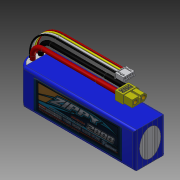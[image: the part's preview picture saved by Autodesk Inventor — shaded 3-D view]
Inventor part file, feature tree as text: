
AUTODESK INVENTOR PART (.ipt)
format: ipt  version: 2014 SP1 (Build 180222100, 222)  size: 2,148,352 bytes
history: native  units: mm
features: sketch x30, extrude x23, plane x4, pattern_linear x3, sweep x3, fillet x2, other x2, emboss x1, projected_geometry x1
ambient origin geometry x8: Origin, YZ Plane, XZ Plane, XY Plane, X Axis, Y Axis, Z Axis, Center Point
bodies: Solid1 (feature_tree)
feature tree (69):
  extrude  "Extrusion1"  Depth=33.0mm
  extrude  "Extrusion2"  Depth=2.0mm
  pattern_linear  "Rectangular Pattern1"  Count1=2 Spacing1=9.333333mm
  fillet  "Fillet1"  Radius=2.0mm
  extrude  "Extrusion3"  Depth=105.0mm TaperAngle=0.0deg
  plane  "Work Plane1"
  extrude  "Extrusion4"  Depth=13.8mm
  extrude  "Extrusion5"  Depth=11.6mm
  extrude  "Extrusion6"  Depth=30.0mm
  extrude  "Extrusion7"  Depth=7.85mm TaperAngle=0.0deg
  extrude  "Extrusion8"  Depth=4.0mm
  extrude  "Extrusion9"  Depth=1.8mm
  plane  "Work Plane2"
  emboss  "Emboss1"
  extrude  "Extrusion10"  Depth=0.75mm
  extrude  "Extrusion11"  Depth=7.6mm TaperAngle=0.0deg
  sketch  "Sketch13"  dims[d32=1.0mm d33=0.0mm d34=1.8mm]
  sketch  "3D Sketch1"
  sweep  "Sweep1"
  sweep  "Sweep2"
  extrude  "Extrusion12"  Depth=60.0mm
  plane  "Work Plane3"
  extrude  "Extrusion13"  Depth=10.0mm TaperAngle=0.0deg
  extrude  "Extrusion14"  Depth=4.3mm
  extrude  "Extrusion15"  Depth=0.3mm TaperAngle=0.0deg
  extrude  "Extrusion16"  Depth=3.5mm
  extrude  "Extrusion17"  Depth=4.0mm
  extrude  "Extrusion18"  Depth=3.9mm
  extrude  "Extrusion19"  Depth=7.8mm
  extrude  "Extrusion20"  Depth=10.0mm
  extrude  "Extrusion21"  Depth=10.0mm
  pattern_linear  "Rectangular Pattern2"  Spacing1=0.0mm  [1 undecoded]
  sketch  "Sketch25"  dims[d74=0.3mm d75=0.0mm d76=3.9mm]
  sweep  "Sweep3"
  pattern_linear  "Rectangular Pattern3"  Spacing1=10.337mm  [1 undecoded]
  extrude  "Extrusion22"  Depth=2.0mm TaperAngle=0.0deg
  plane  "Work Plane4"
  extrude  "Extrusion23"  [1 undecoded]
  fillet  "Fillet4"  Radius=10.6mm
  other  "Decal1"
  sketch  "Sketch1"  dims[d0=28.0mm d1=33.0mm]
  sketch  "Sketch2"  dims[d2=105.0mm d3=0.0mm d4=2.0mm]
  sketch  "Sketch3"  dims[d5=2.0mm]
  sketch  "Sketch4"  dims[d6=28.0mm]
  sketch  "Sketch5"  dims[d7=9.333333mm]
  sketch  "Sketch6"  dims[d8=105.0mm d9=0.0mm d10=20.0mm d12=9.333333mm d13=2.0mm]
  sketch  "Sketch7"  dims[d14=8.0mm d15=105.0mm d16=0.0mm]
  sketch  "Sketch8"  dims[d17=-10.0mm d18=13.8mm]
  sketch  "Sketch9"  dims[d19=6.6mm d20=11.6mm]
  sketch  "Sketch10"  dims[d21=2.2mm d22=30.0mm]
  sketch  "Sketch11"  dims[d26=6.6mm d27=7.85mm d28=0.0mm]
  sketch  "Sketch12"  dims[d29=1.0mm d30=4.0mm]
  sketch  "Sketch14"  dims[d35=1.0mm d36=0.0mm d37=0.75mm]
  sketch  "Sketch15"  dims[d38=0.75mm d39=7.6mm d40=0.0mm]
  sketch  "Sketch16"  dims[d41=10.0mm d42=0.3mm d43=0.0mm]
  sketch  "Sketch17"  dims[d44=0.1mm d45=4.93934mm]
  sketch  "Sketch18"  dims[d46=0.70562mm d54=60.0mm d56=0.70562mm]
  sketch  "Sketch19"  dims[d57=10.0mm d59=10.0mm d61=0.3mm d62=0.0mm]
  sketch  "Sketch20"  dims[d63=1.0mm d64=0.0mm d65=4.3mm]
  sketch  "Sketch21"  dims[d67=3.4mm d68=0.3mm d69=0.0mm]
  sketch  "Sketch22"  dims[d70=3.5mm d71=3.5mm]
  sketch  "Sketch24"  dims[d72=4.0mm d73=4.0mm]
  sketch  "Sketch26"  dims[d77=3.9mm d78=7.8mm]
  sketch  "3D Sketch2"
  sketch  "Sketch27"  dims[d80=10.0mm d81=13.5mm]
  projected_geometry  "Projected Loop1"
  sketch  "Sketch29"  dims[d82=13.5mm d83=10.0mm]
  sketch  "Sketch31"  dims[d84=10.0mm d85=0.0mm d86=0.0mm d87=10.337mm d88=20.0mm d89=0.0mm d90=-10.0mm d91=10.6mm d92=3.9mm d93=42.0mm d94=7.7mm d95=0.0mm d96=5.0mm d97=0.7mm d98=0.0mm d99=1.25mm d100=0.5mm d101=5.8mm d102=2.6mm d103=2.2mm d104=0.5mm d105=0.7mm d106=0.0mm d107=0.7mm d108=0.0mm d109=1.1mm d110=1.1mm d111=0.85mm d112=10.6mm d113=1.79mm d114=40.0mm d116=2.34mm d117=10.0mm d119=10.0mm d121=0.7mm d122=0.0mm d123=3.0mm d124=3.0mm d125=0.0mm d126=1.5mm d127=0.5mm d128=0.0mm d129=0.05mm d130=0.05mm d131=0.5mm d132=0.0mm d136=0.05mm d137=0.05mm d138=0.05mm d139=0.5mm d140=0.0mm d141=40.0mm d143=2.34mm d144=1.4mm d145=1.4mm d146=10.253mm d147=5.0mm d148=28.0mm d149=25.0mm d150=0.0mm d151=40.0mm d153=2.34mm d154=0.2mm d155=0.5mm d156=0.0mm d157=0.1mm d158=10.0mm d159=13.0mm d160=0.1mm d161=0.0mm d166=2.0mm]
  other  "Image1"
note: 3 required parameter values undecoded (feature->parameter linkage not recoverable at this tier; creation-order binding heuristic only, values carry confidence <= 0.55)
